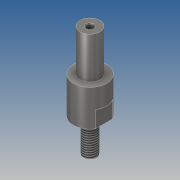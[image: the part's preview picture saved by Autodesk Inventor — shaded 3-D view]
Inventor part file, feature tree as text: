
AUTODESK INVENTOR PART (.ipt)
format: ipt  version: 2018.2 (Build 222227000, 227)  size: 123,392 bytes
history: native  units: mm
features: sketch x3, chamfer x2, other x1, hole x1, extrude x1
ambient origin geometry x8: Origin, YZ Plane, XZ Plane, XY Plane, X Axis, Y Axis, Z Axis, Center Point
bodies: Volumenkörper1 (feature_tree)
feature tree (8):
  other  "Grundkörper"
  hole  "M5x10"  [1 undecoded]
  extrude  "Extrusion1"  Depth=21.8mm
  chamfer  "Fase_Gewinde"  Angle=90.0deg  [1 undecoded]
  chamfer  "Fase_Allgemein"  Distance=10.0mm
  sketch  "Skizze1"  dims[d0=12.0mm d1=25.0mm]
  sketch  "Skizze2"  dims[d3=8.0mm d4=21.8mm]
  sketch  "Skizze3"  dims[d6=20.0mm d7=90.0deg d8=10.0mm d9=0.0mm d10=1.0mm d11=2.0mm d12=45.0deg d13=1.0mm d14=2.0mm d15=45.0deg d16=4.134mm d17=10.0mm d18=5.0mm d19=2.0mm d20=90.0deg d21=14.2mm d22=20.594885mm d23=20.0mm d24=10.0mm d25=17.0mm d26=10.0mm d27=0.0mm]
note: 2 required parameter values undecoded (feature->parameter linkage not recoverable at this tier; creation-order binding heuristic only, values carry confidence <= 0.55)
